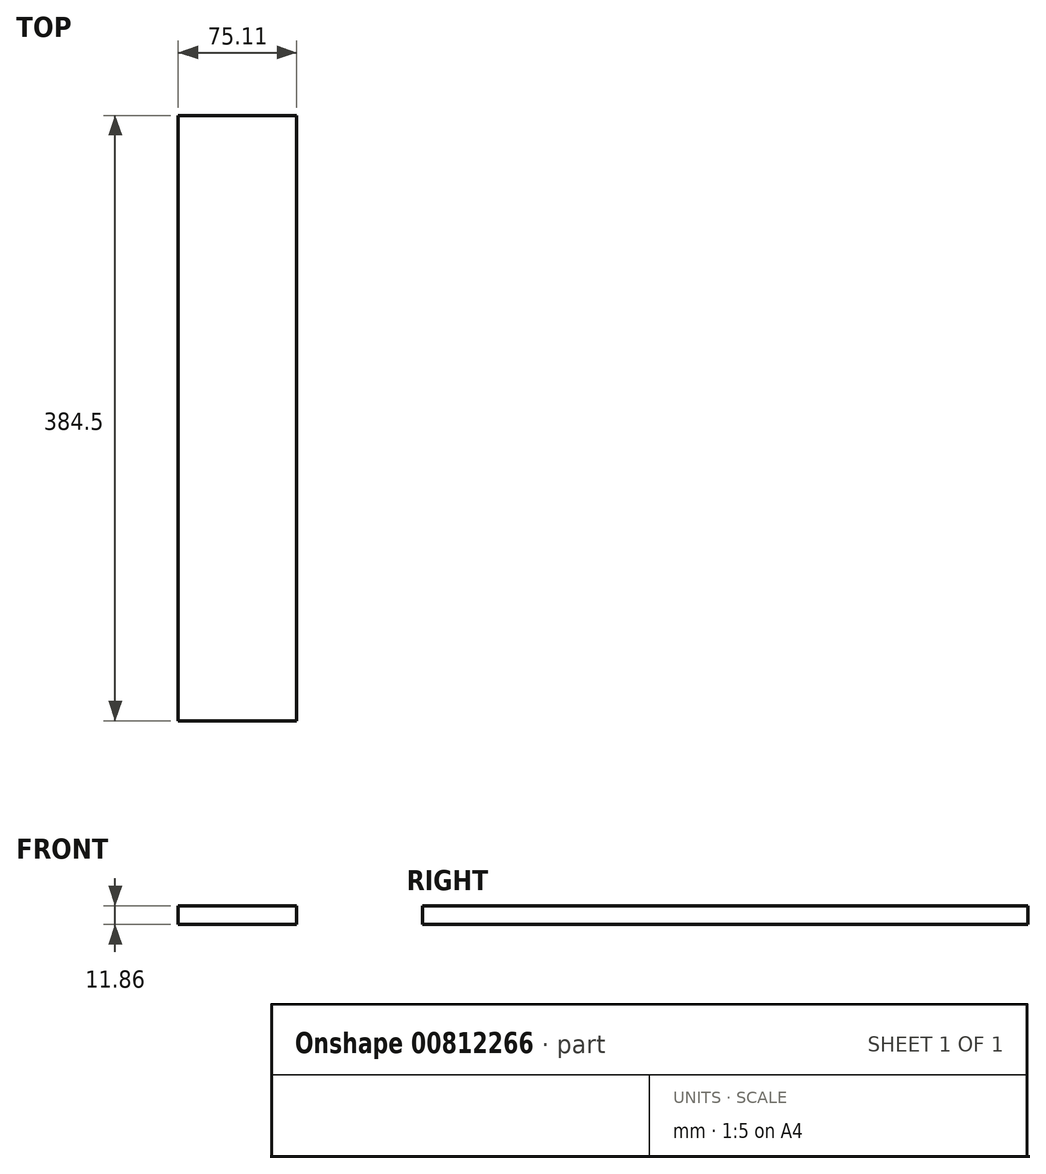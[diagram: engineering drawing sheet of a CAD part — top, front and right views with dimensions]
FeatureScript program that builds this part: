
annotation { "Feature Type Name" : "Feature", "Feature Type Description" : "" }
export const myFeature = defineFeature(function(context is Context, id is Id, definition is map)
    precondition{}
    {
        {
            var Q0;
            Q0=qCreatedBy(makeId("Front.planeOp"),FACE);
            var sketch = newSketch(context, id + "F0", { "sketchPlane" : qUnion([Q0])});
            skLineSegment(sketch, "E0.bottom", {"start": v(-27.83, 11.86) * mm, "end": v(47.28, 11.86) * mm});
            skLineSegment(sketch, "E0.top", {"start": v(-27.83, 0) * mm, "end": v(47.28, 0) * mm});
            skLineSegment(sketch, "E0.left", {"start": v(-27.83, 11.86) * mm, "end": v(-27.83, 0) * mm});
            skLineSegment(sketch, "E0.right", {"start": v(47.28, 11.86) * mm, "end": v(47.28, 0) * mm});
            skSolve(sketch);
        }
        {
            var Q0;
            Q0=makeQuery(id+"F0.imprint","IMPRINT",FACE,{"disambiguationData":[TD([[makeQuery(id+"F0.imprint","IMPRINT",EDGE,{"derivedFrom":sQuery(id+"F0.wireOp",EDGE,"E0.bottom")}),-1.0]])]});
            extrude(context, id + "F1", {"entities" : qUnion([Q0]), "depth" : 74.5 * mm, "offsetDistance" : 25 * mm});
        }
        {
            var Q0;
            Q0=makeQuery(id+"F1.opExtrude","CAP_FACE",FACE,{"disambiguationData":[OSD([sQuery(id+"F0.wireOp",EDGE,"E0.bottom"),sQuery(id+"F0.wireOp",EDGE,"E0.top"),sQuery(id+"F0.wireOp",EDGE,"E0.left"),sQuery(id+"F0.wireOp",EDGE,"E0.right")])],"isStart":true});
            extrude(context, id + "F2", {"entities" : qUnion([Q0]), "operationType" : NewBodyOperationType.ADD, "depth" : 310 * mm, "offsetDistance" : 25 * mm});
        }
    });
